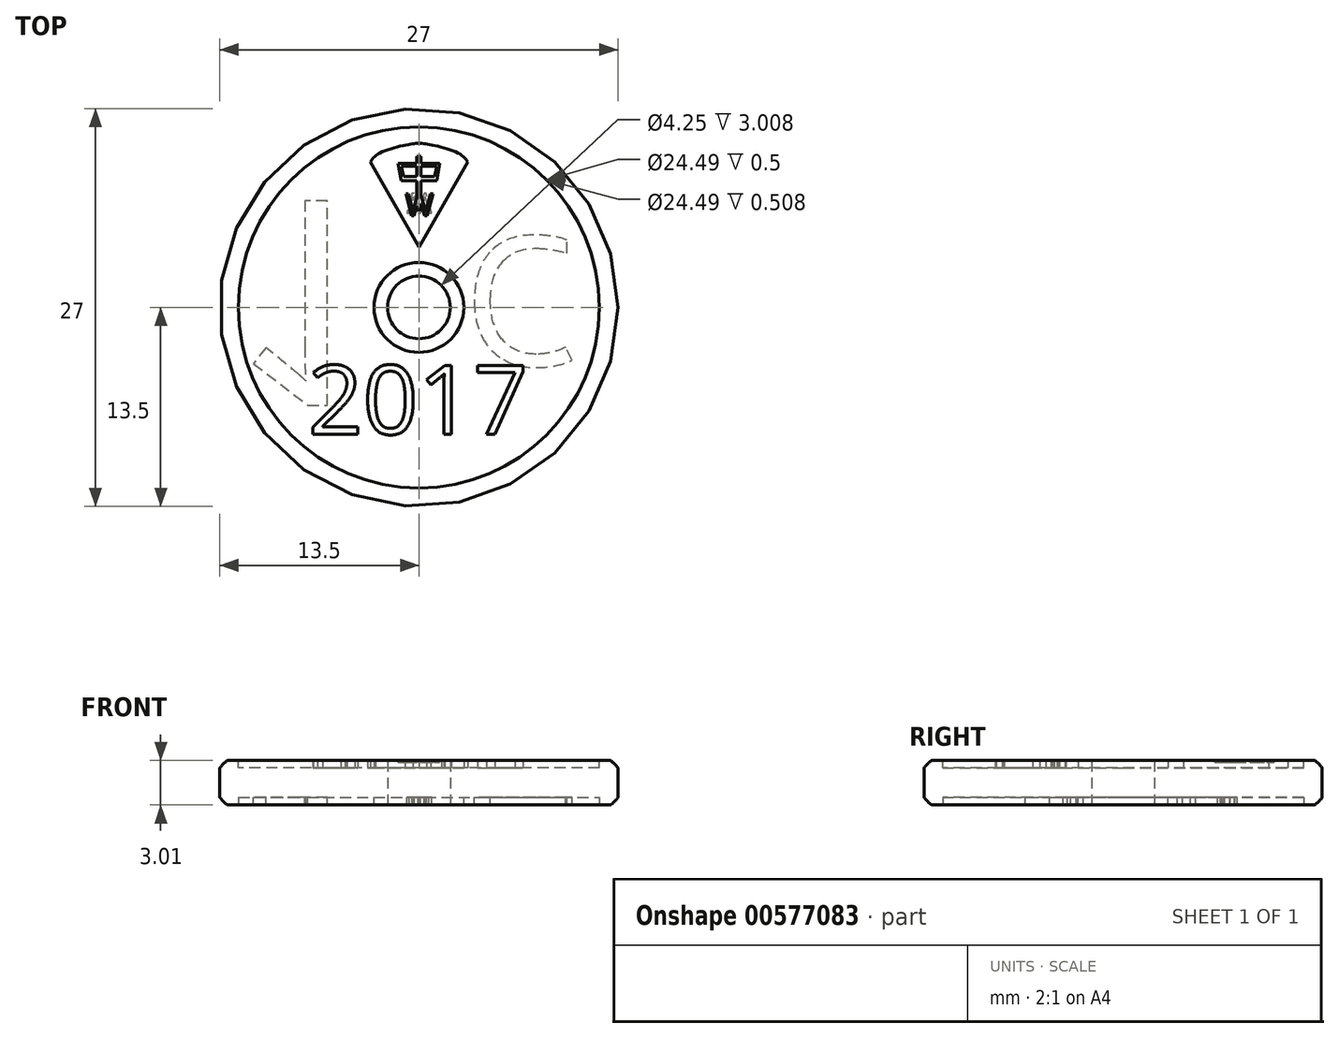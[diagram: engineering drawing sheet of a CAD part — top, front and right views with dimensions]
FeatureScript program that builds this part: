
annotation { "Feature Type Name" : "Feature", "Feature Type Description" : "" }
export const myFeature = defineFeature(function(context is Context, id is Id, definition is map)
    precondition{}
    {
        {
            var Q0;
            Q0=qCreatedBy(makeId("Top.planeOp"),FACE);
            var sketch = newSketch(context, id + "F0", { "sketchPlane" : qUnion([Q0])});
            skCircle(sketch, "E0", {"center": v(0, 0) * mm, "radius": 13.5 * mm});
            skCircle(sketch, "E1", {"center": v(0, 0) * mm, "radius": 2.13 * mm});
            skSolve(sketch);
        }
        {
            var Q0;
            Q0=makeQuery(id+"F0.imprint","IMPRINT",FACE,{"disambiguationData":[TD([[makeQuery(id+"F0.imprint","IMPRINT",EDGE,{"derivedFrom":sQuery(id+"F0.wireOp",EDGE,"E0")}),1.0]])]});
            extrude(context, id + "F1", {"entities" : qUnion([Q0]), "depth" : 3 * mm, "offsetDistance" : 25.4 * mm});
        }
        {
            var Q0;
            Q0=makeQuery(id+"F1.opExtrude","CAP_FACE",FACE,{"disambiguationData":[OSD([sQuery(id+"F0.wireOp",EDGE,"E0"),sQuery(id+"F0.wireOp",EDGE,"E1")])],"isStart":true});
            var sketch = newSketch(context, id + "F2", { "sketchPlane" : qUnion([Q0])});
            skCircle(sketch, "E2", {"center": v(0, 0) * mm, "radius": 12.25 * mm});
            skSolve(sketch);
        }
        {
            var Q0;
            Q0=makeQuery(id+"F1.opExtrude","CAP_FACE",FACE,{"disambiguationData":[OSD([sQuery(id+"F0.wireOp",EDGE,"E0"),sQuery(id+"F0.wireOp",EDGE,"E1")])],"isStart":false});
            var sketch = newSketch(context, id + "F3", { "sketchPlane" : qUnion([Q0])});
            skCircle(sketch, "E3", {"center": v(0, 0) * mm, "radius": 12.25 * mm});
            skSolve(sketch);
        }
        {
            var Q0;
            Q0=makeQuery(id+"F2.imprint","IMPRINT",FACE,{"disambiguationData":[TD([[makeQuery(id+"F2.imprint","IMPRINT",EDGE,{"derivedFrom":sQuery(id+"F2.wireOp",EDGE,"E2")}),1.0]])]});
            extrude(context, id + "F4", {"entities" : qUnion([Q0]), "operationType" : NewBodyOperationType.REMOVE, "oppositeDirection" : true, "depth" : 0.5 * mm, "offsetDistance" : 25.4 * mm});
        }
        {
            var Q0;
            Q0=makeQuery(id+"F3.imprint","IMPRINT",FACE,{"disambiguationData":[TD([[makeQuery(id+"F3.imprint","IMPRINT",EDGE,{"derivedFrom":sQuery(id+"F3.wireOp",EDGE,"E3")}),1.0]])]});
            extrude(context, id + "F5", {"entities" : qUnion([Q0]), "operationType" : NewBodyOperationType.REMOVE, "oppositeDirection" : true, "depth" : 0.5 * mm, "offsetDistance" : 25.4 * mm});
        }
        {
            var Q0;
            Q0=makeQuery(id+"F4.boolean.opBoolean","COPY",FACE,{"derivedFrom":makeQuery(id+"F4.opExtrude","CAP_FACE",FACE,{"disambiguationData":[OSD([sQuery(id+"F0.wireOp",EDGE,"E1"),sQuery(id+"F2.wireOp",EDGE,"E2")])],"isStart":false})});
            var sketch = newSketch(context, id + "F6", { "sketchPlane" : qUnion([Q0])});
            skCircle(sketch, "E4", {"center": v(0, 0) * mm, "radius": 3.05 * mm});
            skSolve(sketch);
        }
        {
            var Q0;
            Q0=makeQuery(id+"F5.boolean.opBoolean","COPY",FACE,{"derivedFrom":makeQuery(id+"F5.opExtrude","CAP_FACE",FACE,{"disambiguationData":[OSD([sQuery(id+"F0.wireOp",EDGE,"E1"),sQuery(id+"F3.wireOp",EDGE,"E3")])],"isStart":false})});
            var sketch = newSketch(context, id + "F7", { "sketchPlane" : qUnion([Q0])});
            skCircle(sketch, "E5", {"center": v(0, 0) * mm, "radius": 3.05 * mm});
            skSolve(sketch);
        }
        {
            var Q0;
            Q0=makeQuery(id+"F7.imprint","IMPRINT",FACE,{"disambiguationData":[TD([[makeQuery(id+"F7.imprint","IMPRINT",EDGE,{"derivedFrom":sQuery(id+"F7.wireOp",EDGE,"E5")}),1.0]])]});
            extrude(context, id + "F8", {"entities" : qUnion([Q0]), "operationType" : NewBodyOperationType.ADD, "depth" : 0.5 * mm, "offsetDistance" : 25.4 * mm});
        }
        {
            var Q0;
            Q0=makeQuery(id+"F6.imprint","IMPRINT",FACE,{"disambiguationData":[TD([[makeQuery(id+"F6.imprint","IMPRINT",EDGE,{"derivedFrom":sQuery(id+"F6.wireOp",EDGE,"E4")}),1.0]])]});
            extrude(context, id + "F9", {"entities" : qUnion([Q0]), "operationType" : NewBodyOperationType.ADD, "depth" : 0.5 * mm, "offsetDistance" : 25.4 * mm});
        }
        {
            var Q0;
            Q0=makeQuery(id+"F4.boolean.opBoolean","COPY",FACE,{"derivedFrom":makeQuery(id+"F4.opExtrude","CAP_FACE",FACE,{"disambiguationData":[OSD([sQuery(id+"F0.wireOp",EDGE,"E1"),sQuery(id+"F2.wireOp",EDGE,"E2")])],"isStart":false})});
            var sketch = newSketch(context, id + "F10", { "sketchPlane" : qUnion([Q0])});
            skSolve(sketch);
        }
        {
            var Q0;
            Q0=makeQuery(id+"F5.boolean.opBoolean","COPY",FACE,{"derivedFrom":makeQuery(id+"F5.opExtrude","CAP_FACE",FACE,{"disambiguationData":[OSD([sQuery(id+"F0.wireOp",EDGE,"E1"),sQuery(id+"F3.wireOp",EDGE,"E3")])],"isStart":false})});
            var sketch = newSketch(context, id + "F11", { "sketchPlane" : qUnion([Q0])});
            skText(sketch, "E6", { "text": "2017", "fontName": "OpenSans-Regular.ttf"});
            const initialGuessF11  = {"E6": [-0.00753, -0.0086, 1, 0, 0.0047]};
            skSetInitialGuess(sketch, initialGuessF11);
            skSolve(sketch);
        }
        {
            var Q0;
            Q0 = qSketchRegion(id + "F11", true);
            extrude(context, id + "F12", {"entities" : qUnion([Q0]), "operationType" : NewBodyOperationType.ADD, "depth" : 0.5 * mm, "offsetDistance" : 25.4 * mm});
        }
        {
            var Q0;
            Q0=makeQuery(id+"F1.opExtrude","CAP_EDGE",EDGE,{"disambiguationData":[OSD([sQuery(id+"F0.wireOp",EDGE,"E0")])],"isStart":false});
            fillet(context, id + "F13", {"entities" : qUnion([Q0]), "radius" : 0.5 * mm, "rho" : 0.1, "crossSection" : FilletCrossSection.CONIC, "allowEdgeOverflow" : false});
        }
        {
            var Q0;
            Q0=makeQuery(id+"F1.opExtrude","CAP_EDGE",EDGE,{"disambiguationData":[OSD([sQuery(id+"F0.wireOp",EDGE,"E0")])],"isStart":true});
            fillet(context, id + "F14", {"entities" : qUnion([Q0]), "radius" : 0.5 * mm, "rho" : 0.1, "crossSection" : FilletCrossSection.CONIC, "allowEdgeOverflow" : false});
        }
        {
            var Q0;
            {var subQ0=sQuery(id+"F3.wireOp",EDGE,"E3");Q0=makeQuery(id+"F12.boolean.opBoolean","SPLIT",FACE,{"disambiguationData":[TD([makeQuery(id+"F5.boolean.opBoolean","COPY",FACE,{"derivedFrom":makeQuery(id+"F5.opExtrude","SWEPT_FACE",FACE,{"disambiguationData":[OSD([subQ0])]})})])],"derivedFrom":makeQuery(id+"F5.boolean.opBoolean","COPY",FACE,{"derivedFrom":makeQuery(id+"F5.opExtrude","CAP_FACE",FACE,{"disambiguationData":[OSD([sQuery(id+"F0.wireOp",EDGE,"E1"),subQ0])],"isStart":false})})});}
            var sketch = newSketch(context, id + "F15", { "sketchPlane" : qUnion([Q0])});
            skFitSpline(sketch, "E7", {"points": [v(0, 11.15) * mm, v(-0.8, 11.04) * mm, v(-2.74, 10.43) * mm, v(-3.3, 9.87) * mm], "startDerivative": vector(-2.37, -0.23) * mm, "endDerivative": vector(-1.42, -2.09) * mm});
            skLineSegment(sketch, "E8", {"start": v(-3.3, 9.87) * mm, "end": v(0, 4.09) * mm});
            skFitSpline(sketch, "E9.MirrorCS", {"points": [v(0, 11.15) * mm, v(0.8, 11.04) * mm, v(2.74, 10.43) * mm, v(3.3, 9.87) * mm], "startDerivative": vector(2.37, -0.23) * mm, "endDerivative": vector(1.42, -2.09) * mm});
            skLineSegment(sketch, "E10.MirrorCS", {"start": v(3.3, 9.87) * mm, "end": v(0, 4.09) * mm});
            skSolve(sketch);
        }
        {
            var Q0;
            Q0=makeQuery(id+"F15.imprint","IMPRINT",FACE,{"disambiguationData":[TD([[makeQuery(id+"F15.imprint","IMPRINT",EDGE,{"derivedFrom":sQuery(id+"F15.wireOp",EDGE,"E7")}),1.0]])]});
            extrude(context, id + "F16", {"entities" : qUnion([Q0]), "operationType" : NewBodyOperationType.ADD, "depth" : 0.5 * mm, "offsetDistance" : 25.4 * mm});
        }
        {
            var Q0;
            Q0=makeQuery(id+"F16.opExtrude","CAP_FACE",FACE,{"disambiguationData":[OSD([sQuery(id+"F15.wireOp",EDGE,"E7"),sQuery(id+"F15.wireOp",EDGE,"E8"),sQuery(id+"F15.wireOp",EDGE,"E9.MirrorCS"),sQuery(id+"F15.wireOp",EDGE,"E10.MirrorCS")])],"isStart":false});
            var sketch = newSketch(context, id + "F17", { "sketchPlane" : qUnion([Q0])});
            skText(sketch, "E11", { "text": "W", "fontName": "OpenSans-Regular.ttf"});
            skLineSegment(sketch, "E12", {"start": v(0, 6.62) * mm, "end": v(-0.14, 6.62) * mm});
            skLineSegment(sketch, "E13", {"start": v(-0.14, 6.62) * mm, "end": v(-0.14, 8.6) * mm});
            skLineSegment(sketch, "E14", {"start": v(-0.14, 8.6) * mm, "end": v(-1.2, 8.6) * mm});
            skLineSegment(sketch, "E15", {"start": v(-1.2, 8.6) * mm, "end": v(-1.42, 9.78) * mm});
            skLineSegment(sketch, "E16", {"start": v(-1.42, 9.78) * mm, "end": v(-0.14, 9.78) * mm});
            skLineSegment(sketch, "E17", {"start": v(-0.14, 9.78) * mm, "end": v(-0.14, 10.25) * mm});
            skLineSegment(sketch, "E18", {"start": v(-0.14, 10.25) * mm, "end": v(0, 10.25) * mm});
            skLineSegment(sketch, "E19.MirrorCS", {"start": v(0.14, 9.78) * mm, "end": v(0.14, 10.25) * mm});
            skLineSegment(sketch, "E20.MirrorCS", {"start": v(0.14, 10.25) * mm, "end": v(0, 10.25) * mm});
            skLineSegment(sketch, "E21.MirrorCS", {"start": v(1.2, 8.6) * mm, "end": v(1.42, 9.78) * mm});
            skLineSegment(sketch, "E22.MirrorCS", {"start": v(1.42, 9.78) * mm, "end": v(0.14, 9.78) * mm});
            skLineSegment(sketch, "E23.MirrorCS", {"start": v(0.14, 6.62) * mm, "end": v(0.14, 8.6) * mm});
            skLineSegment(sketch, "E24.MirrorCS", {"start": v(0.14, 8.6) * mm, "end": v(1.2, 8.6) * mm});
            skLineSegment(sketch, "E25.MirrorCS", {"start": v(0, 6.62) * mm, "end": v(0.14, 6.62) * mm});
            skLineSegment(sketch, "E26", {"start": v(-1.2, 9.58) * mm, "end": v(-0.15, 9.58) * mm});
            skLineSegment(sketch, "E27", {"start": v(-0.15, 9.58) * mm, "end": v(-0.15, 8.9) * mm});
            skLineSegment(sketch, "E28", {"start": v(-0.15, 8.9) * mm, "end": v(-1.05, 8.9) * mm});
            skLineSegment(sketch, "E29", {"start": v(-1.05, 8.9) * mm, "end": v(-1.2, 9.58) * mm});
            skLineSegment(sketch, "E30.MirrorCS", {"start": v(0.15, 9.58) * mm, "end": v(0.15, 8.9) * mm});
            skLineSegment(sketch, "E31.MirrorCS", {"start": v(1.2, 9.58) * mm, "end": v(0.15, 9.58) * mm});
            skLineSegment(sketch, "E32.MirrorCS", {"start": v(1.05, 8.9) * mm, "end": v(1.2, 9.58) * mm});
            skLineSegment(sketch, "E33.MirrorCS", {"start": v(0.15, 8.9) * mm, "end": v(1.05, 8.9) * mm});
            const initialGuessF17  = {"E11": [-0.00092, 0.00623, 1, 0, 0.00148]};
            skSetInitialGuess(sketch, initialGuessF17);
            skSolve(sketch);
        }
        {
            var Q0;
            {var subQ5=sQuery(id+"F17.wireOp",EDGE,"E11.sketch_text.stroke-0");Q0=makeQuery(id+"F17.imprint","IMPRINT",FACE,{"disambiguationData":[TD([[makeQuery(id+"F17.imprint","IMPRINT",EDGE,{"derivedFrom":subQ5}),-1.0]])]});}
            var Q1;
            {var subQ0=sQuery(id+"F17.wireOp",EDGE,"E11.sketch_text.stroke-6");Q1=makeQuery(id+"F17.imprint","IMPRINT",FACE,{"disambiguationData":[TD([[makeQuery(id+"F17.imprint","IMPRINT",EDGE,{"derivedFrom":subQ0}),-1.0]])]});}
            var Q2;
            {var subQ8=sQuery(id+"F17.wireOp",EDGE,"E11.sketch_text.stroke-13");Q2=makeQuery(id+"F17.imprint","IMPRINT",FACE,{"disambiguationData":[TD([[makeQuery(id+"F17.imprint","IMPRINT",EDGE,{"derivedFrom":subQ8}),1.0]])]});}
            var Q3;
            {var subQ5=sQuery(id+"F17.wireOp",EDGE,"E11.sketch_text.stroke-2");Q3=makeQuery(id+"F17.imprint","IMPRINT",FACE,{"disambiguationData":[TD([[makeQuery(id+"F17.imprint","IMPRINT",EDGE,{"derivedFrom":subQ5}),1.0]])]});}
            var Q4;
            {var subQ12=sQuery(id+"F17.wireOp",EDGE,"E11.sketch_text.stroke-2");Q4=makeQuery(id+"F17.imprint","IMPRINT",FACE,{"disambiguationData":[TD([[makeQuery(id+"F17.imprint","IMPRINT",EDGE,{"derivedFrom":subQ12}),-1.0]])]});}
            extrude(context, id + "F18", {"entities" : qUnion([Q0, Q1, Q2, Q3, Q4]), "operationType" : NewBodyOperationType.REMOVE, "oppositeDirection" : true, "depth" : 0.13 * mm, "offsetDistance" : 25.4 * mm});
        }
        {
            var Q0;
            Q0=makeQuery(id+"F10.imprint","IMPRINT",FACE,{"disambiguationData":[TD([[makeQuery(id+"F10.imprint","IMPRINT",EDGE,{"derivedFrom":makeQuery(id+"F4.boolean.opBoolean","COPY",EDGE,{"derivedFrom":makeQuery(id+"F4.opExtrude","CAP_EDGE",EDGE,{"disambiguationData":[OSD([sQuery(id+"F2.wireOp",EDGE,"E2")])],"isStart":false})})}),1.0]])]});
            var sketch = newSketch(context, id + "F19", { "sketchPlane" : qUnion([Q0])});
            skText(sketch, "E34", { "text": "1", "fontName": "OpenSans-Regular.ttf"});
            skText(sketch, "E35", { "text": "C", "fontName": "OpenSans-Regular.ttf"});
            const initialGuessF19  = {"E34": [-0.013, -0.00724, 1, 0, 0.014], "E35": [0.00301, -0.0048, 1, 0, 0.00883]};
            skSetInitialGuess(sketch, initialGuessF19);
            skSolve(sketch);
        }
        {
            var Q0;
            Q0 = qSketchRegion(id + "F19", true);
            extrude(context, id + "F20", {"entities" : qUnion([Q0]), "operationType" : NewBodyOperationType.ADD, "depth" : 0.5 * mm, "offsetDistance" : 25.4 * mm});
        }
        {
            var Q0;
            Q0=makeQuery(id+"F10.imprint","IMPRINT",FACE,{"disambiguationData":[TD([[makeQuery(id+"F10.imprint","IMPRINT",EDGE,{"derivedFrom":makeQuery(id+"F4.boolean.opBoolean","COPY",EDGE,{"derivedFrom":makeQuery(id+"F4.opExtrude","CAP_EDGE",EDGE,{"disambiguationData":[OSD([sQuery(id+"F2.wireOp",EDGE,"E2")])],"isStart":false})})}),1.0]])]});
            var sketch = newSketch(context, id + "F21", { "sketchPlane" : qUnion([Q0])});
            skFitSpline(sketch, "E36", {"points": [v(0, 9.15) * mm, v(-1.73, 8.97) * mm, v(-3.5, 8.18) * mm, v(-5.63, 7.57) * mm, v(-6.49, 8.79) * mm, v(0, 10.74) * mm], "startDerivative": vector(-10.73, -0.35) * mm, "endDerivative": vector(28.53, 4.39) * mm});
            skFitSpline(sketch, "E37", {"points": [v(0, -8.4) * mm, v(-3, -9.13) * mm, v(-4.17, -8.1) * mm, v(0, -5.53) * mm], "startDerivative": vector(-9.36, -4.06) * mm, "endDerivative": vector(14.43, 6.16) * mm});
            skFitSpline(sketch, "E38", {"points": [v(0, -4.51) * mm, v(-3.92, -6.22) * mm, v(-5.27, -8) * mm, v(-4.66, -9.64) * mm, v(-1.55, -10.13) * mm, v(0, -9.82) * mm], "startDerivative": vector(-16.75, -5.82) * mm, "endDerivative": vector(8.26, 2.33) * mm});
            skFitSpline(sketch, "E39.MirrorCS", {"points": [v(0, 9.15) * mm, v(1.73, 8.97) * mm, v(3.5, 8.18) * mm, v(5.63, 7.57) * mm, v(6.49, 8.79) * mm, v(0, 10.74) * mm], "startDerivative": vector(10.73, -0.35) * mm, "endDerivative": vector(-28.53, 4.39) * mm});
            skFitSpline(sketch, "E40.MirrorCS", {"points": [v(0, -4.51) * mm, v(3.92, -6.22) * mm, v(5.27, -8) * mm, v(4.66, -9.64) * mm, v(1.55, -10.13) * mm, v(0, -9.82) * mm], "startDerivative": vector(16.75, -5.82) * mm, "endDerivative": vector(-8.26, 2.33) * mm});
            skFitSpline(sketch, "E41.MirrorCS", {"points": [v(0, -8.4) * mm, v(3, -9.13) * mm, v(4.17, -8.1) * mm, v(0, -5.53) * mm], "startDerivative": vector(9.36, -4.06) * mm, "endDerivative": vector(-14.43, 6.16) * mm});
            skText(sketch, "E42", { "text": "W", "fontName": "OpenSans-Regular.ttf"});
            const initialGuessF21  = {"E42": [-0.00083, -0.00773, 1, 0, 0.00133]};
            skSetInitialGuess(sketch, initialGuessF21);
            skSolve(sketch);
        }
        {
            var Q0;
            Q0=makeQuery(id+"F21.imprint","IMPRINT",FACE,{"disambiguationData":[TD([[makeQuery(id+"F21.imprint","IMPRINT",EDGE,{"derivedFrom":sQuery(id+"F21.wireOp",EDGE,"E42.sketch_text.stroke-0")}),-1.0]])]});
            extrude(context, id + "F22", {"entities" : qUnion([Q0]), "operationType" : NewBodyOperationType.ADD, "depth" : 0.5 * mm, "offsetDistance" : 25.4 * mm});
        }
    });
